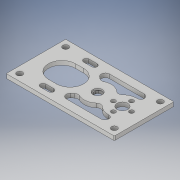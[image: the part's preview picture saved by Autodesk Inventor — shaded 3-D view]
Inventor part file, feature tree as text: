
AUTODESK INVENTOR PART (.ipt)
format: ipt  version: 2018 (Build 220112000, 112)  size: 193,536 bytes
history: native  units: in
note: dims shown in document units (in); Inventor stores cm internally (conversion verified against a paired STEP export)
features: fillet x1
ambient origin geometry x8: Origin, YZ Plane, XZ Plane, XY Plane, X Axis, Y Axis, Z Axis, Center Point
bodies: Solid1 (feature_tree)
feature tree (1):
  fillet  "Fillet3"  [1 undecoded]
note: 1 required parameter value undecoded (feature->parameter linkage not recoverable at this tier; creation-order binding heuristic only, values carry confidence <= 0.55)
